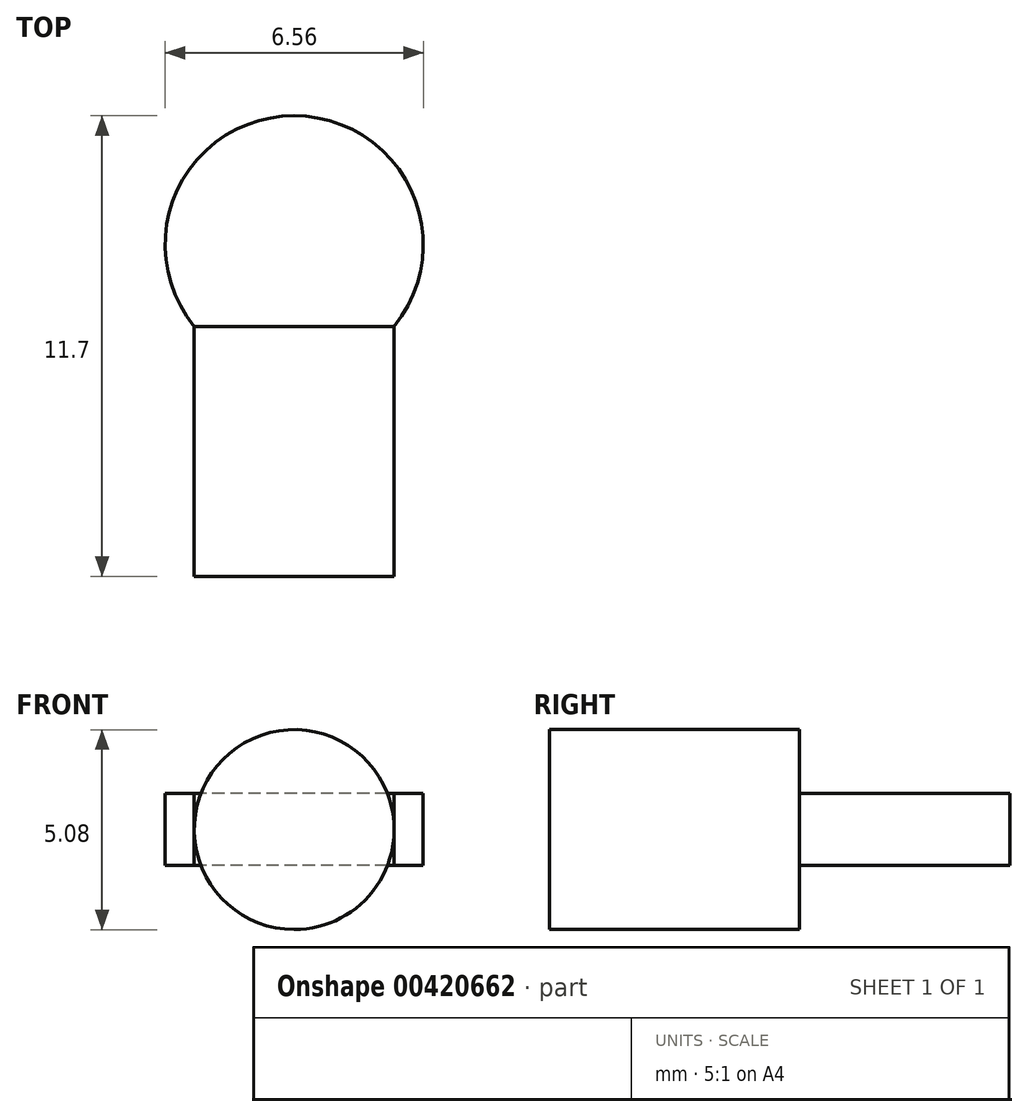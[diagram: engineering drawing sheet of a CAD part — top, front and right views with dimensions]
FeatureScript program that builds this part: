
annotation { "Feature Type Name" : "Feature", "Feature Type Description" : "" }
export const myFeature = defineFeature(function(context is Context, id is Id, definition is map)
    precondition{}
    {
        {
            var Q0;
            Q0=qCreatedBy(makeId("Front.planeOp"),FACE);
            var sketch = newSketch(context, id + "F0", { "sketchPlane" : qUnion([Q0])});
            skCircle(sketch, "E0", {"center": v(-3.78, 2.15) * mm, "radius": 2.54 * mm});
            skSolve(sketch);
        }
        {
            var Q0;
            Q0 = qSketchRegion(id + "F0", true);
            extrude(context, id + "F1", {"entities" : qUnion([Q0]), "depth" : 6.35 * mm});
        }
        {
            var Q0;
            Q0=makeQuery(id+"F1.opExtrude","CAP_FACE",FACE,{"disambiguationData":[OSD([sQuery(id+"F0.wireOp",EDGE,"E0")])],"isStart":true});
            var sketch = newSketch(context, id + "F2", { "sketchPlane" : qUnion([Q0])});
            skLineSegment(sketch, "E1", {"start": v(3.78, 2.15) * mm, "end": v(1.24, 2.15) * mm});
            skLineSegment(sketch, "E2", {"start": v(1.24, 2.15) * mm, "end": v(6.32, 2.15) * mm});
            skSolve(sketch);
        }
        {
            var Q0;
            Q0=sQuery(id+"F2.wireOp",EDGE,"E2");
            cPlane(context, id + "F3", {"entities" : qUnion([Q0]), "cplaneType" : CPlaneType.LINE_ANGLE, "offset" : 25.4 * mm, "angle" : 90 * degree, "width" : 152.4 * mm, "height" : 152.4 * mm});
        }
        {
            var Q0;
            Q0=qCreatedBy(id+"F3.planeOp",FACE);
            var sketch = newSketch(context, id + "F4", { "sketchPlane" : qUnion([Q0])});
            skLineSegment(sketch, "E3.0", {"start": v(-1.24, 0) * mm, "end": v(-6.32, 0) * mm});
            skArc(sketch, "E4", {"start": v(-1.24, 0) * mm, "mid": v(-3.78, 5.35) * mm, "end": v(-6.32, 0) * mm});
            skSolve(sketch);
        }
        {
            var Q0;
            Q0 = qSketchRegion(id + "F4", true);
            extrude(context, id + "F5", {"entities" : qUnion([Q0]), "operationType" : NewBodyOperationType.ADD, "endBound" : BoundingType.SYMMETRIC, "depth" : 1.83 * mm});
        }
    });
